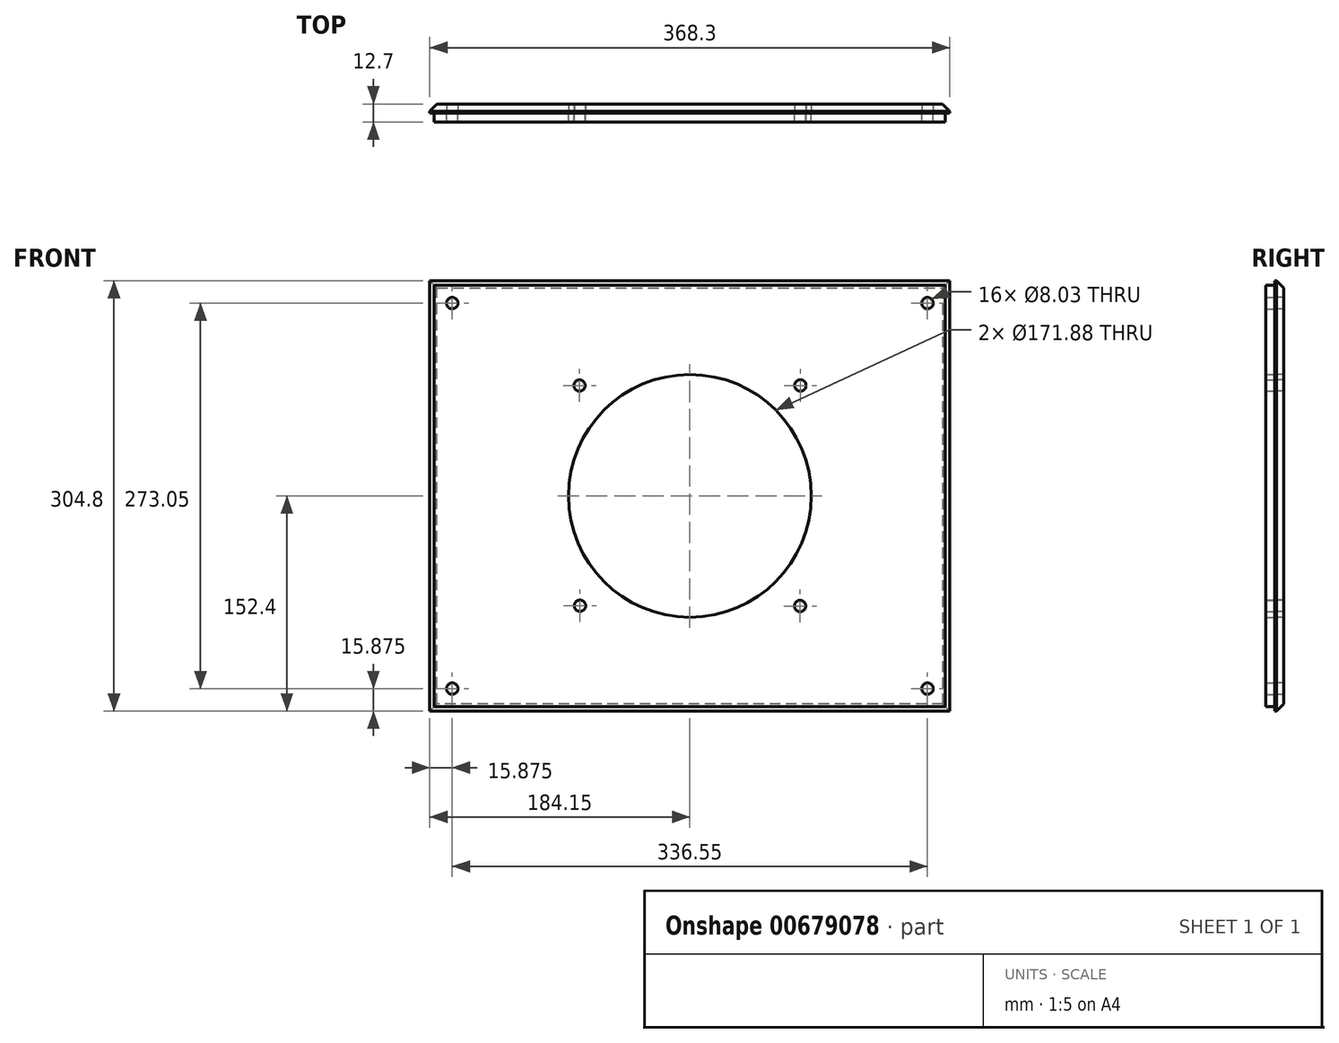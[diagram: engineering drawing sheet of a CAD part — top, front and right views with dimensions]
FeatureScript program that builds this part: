
annotation { "Feature Type Name" : "Feature", "Feature Type Description" : "" }
export const myFeature = defineFeature(function(context is Context, id is Id, definition is map)
    precondition{}
    {
        {
            var Q0;
            Q0=qCreatedBy(makeId("Front.planeOp"),FACE);
            var sketch = newSketch(context, id + "F0", { "sketchPlane" : qUnion([Q0])});
            skLineSegment(sketch, "E0.bottom", {"start": v(-184.15, -152.4) * mm, "end": v(184.15, -152.4) * mm});
            skLineSegment(sketch, "E0.top", {"start": v(-184.15, 152.4) * mm, "end": v(184.15, 152.4) * mm});
            skLineSegment(sketch, "E0.left", {"start": v(-184.15, -152.4) * mm, "end": v(-184.15, 152.4) * mm});
            skLineSegment(sketch, "E0.right", {"start": v(184.15, -152.4) * mm, "end": v(184.15, 152.4) * mm});
            skPoint(sketch, "E0.middle", {"position": v(0, 0) * mm});
            skLineSegment(sketch, "E1.bottom", {"start": v(-180.97, 149.23) * mm, "end": v(180.98, 149.23) * mm});
            skLineSegment(sketch, "E1.top", {"start": v(-180.98, -149.23) * mm, "end": v(180.97, -149.23) * mm});
            skLineSegment(sketch, "E1.left", {"start": v(-180.97, 149.23) * mm, "end": v(-180.98, -149.23) * mm});
            skLineSegment(sketch, "E1.right", {"start": v(180.98, 149.23) * mm, "end": v(180.98, -149.23) * mm});
            skCircle(sketch, "E2", {"center": v(-78.15, 78.2) * mm, "radius": 4.02 * mm});
            skCircle(sketch, "E3", {"center": v(78.22, 78.22) * mm, "radius": 4.02 * mm});
            skCircle(sketch, "E4", {"center": v(78.07, -77.99) * mm, "radius": 4.02 * mm});
            skCircle(sketch, "E5", {"center": v(-77.85, -77.82) * mm, "radius": 4.02 * mm});
            skCircle(sketch, "E6", {"center": v(0, 0) * mm, "radius": 85.94 * mm});
            skCircle(sketch, "E7", {"center": v(-168.28, 136.53) * mm, "radius": 4.02 * mm});
            skCircle(sketch, "E8", {"center": v(-168.28, -136.53) * mm, "radius": 4.02 * mm});
            skCircle(sketch, "E9", {"center": v(168.28, -136.53) * mm, "radius": 4.02 * mm});
            skCircle(sketch, "E10", {"center": v(168.28, 136.53) * mm, "radius": 4.02 * mm});
            skSolve(sketch);
        }
        {
            var Q0;
            Q0=makeQuery(id+"F0.imprint","IMPRINT",FACE,{"disambiguationData":[TD([[makeQuery(id+"F0.imprint","IMPRINT",EDGE,{"derivedFrom":sQuery(id+"F0.wireOp",EDGE,"E1.bottom")}),-1.0]])]});
            extrude(context, id + "F1", {"entities" : qUnion([Q0]), "depth" : 6.35 * mm, "offsetDistance" : 25.4 * mm});
        }
        {
            var Q0;
            Q0=makeQuery(id+"F0.imprint","IMPRINT",FACE,{"disambiguationData":[TD([[makeQuery(id+"F0.imprint","IMPRINT",EDGE,{"derivedFrom":sQuery(id+"F0.wireOp",EDGE,"E0.bottom")}),1.0]])]});
            var Q1;
            Q1=makeQuery(id+"F0.imprint","IMPRINT",FACE,{"disambiguationData":[TD([[makeQuery(id+"F0.imprint","IMPRINT",EDGE,{"derivedFrom":sQuery(id+"F0.wireOp",EDGE,"E1.bottom")}),-1.0]])]});
            extrude(context, id + "F2", {"entities" : qUnion([Q0, Q1]), "depth" : -6.35 * mm, "offsetDistance" : 25.4 * mm});
        }
        {
            var Q0;
            Q0=makeQuery(id+"F2.opExtrude","CAP_EDGE",EDGE,{"disambiguationData":[OSD([sQuery(id+"F0.wireOp",EDGE,"E0.right")])],"isStart":false});
            var Q1;
            Q1=makeQuery(id+"F2.opExtrude","CAP_EDGE",EDGE,{"disambiguationData":[OSD([sQuery(id+"F0.wireOp",EDGE,"E0.top")])],"isStart":false});
            var Q2;
            Q2=makeQuery(id+"F2.opExtrude","CAP_EDGE",EDGE,{"disambiguationData":[OSD([sQuery(id+"F0.wireOp",EDGE,"E0.bottom")])],"isStart":false});
            var Q3;
            Q3=makeQuery(id+"F2.opExtrude","CAP_EDGE",EDGE,{"disambiguationData":[OSD([sQuery(id+"F0.wireOp",EDGE,"E0.left")])],"isStart":false});
            chamfer(context, id + "F3", {"entities" : qUnion([Q0, Q1, Q2, Q3]), "width" : 5.08 * mm, "tangentPropagation" : true});
        }
    });
